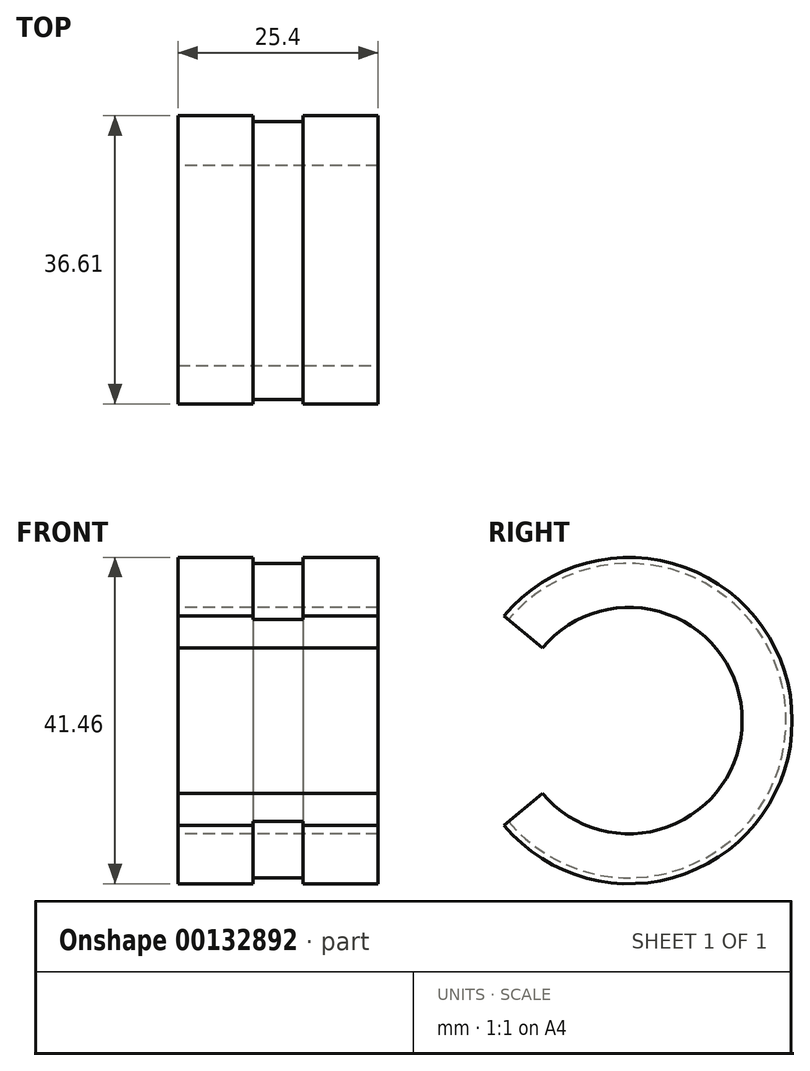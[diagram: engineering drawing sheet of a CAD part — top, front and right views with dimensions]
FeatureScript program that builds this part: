
annotation { "Feature Type Name" : "Feature", "Feature Type Description" : "" }
export const myFeature = defineFeature(function(context is Context, id is Id, definition is map)
    precondition{}
    {
        {
            var Q0;
            Q0=qCreatedBy(makeId("Top.planeOp"),FACE);
            var sketch = newSketch(context, id + "F0", { "sketchPlane" : qUnion([Q0])});
            skLineSegment(sketch, "E0", {"start": v(-53.44, 0) * mm, "end": v(51.7, 0) * mm, "construction": true});
            skLineSegment(sketch, "E1.bottom", {"start": v(-34.27, 20.73) * mm, "end": v(-24.75, 20.73) * mm});
            skLineSegment(sketch, "E1.top", {"start": v(-34.27, 14.38) * mm, "end": v(-8.87, 14.38) * mm});
            skLineSegment(sketch, "E1.left", {"start": v(-34.27, 20.73) * mm, "end": v(-34.27, 14.38) * mm});
            skLineSegment(sketch, "E1.right", {"start": v(-8.87, 20.73) * mm, "end": v(-8.87, 14.38) * mm});
            skLineSegment(sketch, "E2", {"start": v(-24.75, 20.73) * mm, "end": v(-24.75, 19.96) * mm});
            skLineSegment(sketch, "E3", {"start": v(-24.75, 19.96) * mm, "end": v(-18.4, 19.96) * mm});
            skLineSegment(sketch, "E4", {"start": v(-18.4, 19.96) * mm, "end": v(-18.4, 20.73) * mm});
            skLineSegment(sketch, "E5.trimOffspring", {"start": v(-18.4, 20.73) * mm, "end": v(-8.87, 20.73) * mm});
            skSolve(sketch);
        }
        {
            var Q0;
            Q0=makeQuery(id+"F0.imprint","IMPRINT",FACE,{"disambiguationData":[TD([[makeQuery(id+"F0.imprint","IMPRINT",EDGE,{"derivedFrom":sQuery(id+"F0.wireOp",EDGE,"E1.bottom")}),-1.0]])]});
            var Q1;
            Q1=sQuery(id+"F0.wireOp",EDGE,"E0");
            revolve(context, id + "F1", {"entities" : qUnion([Q0]), "axis" : qUnion([Q1]), "revolveType" : RevolveType.SYMMETRIC, "angle" : 280 * degree});
        }
    });
